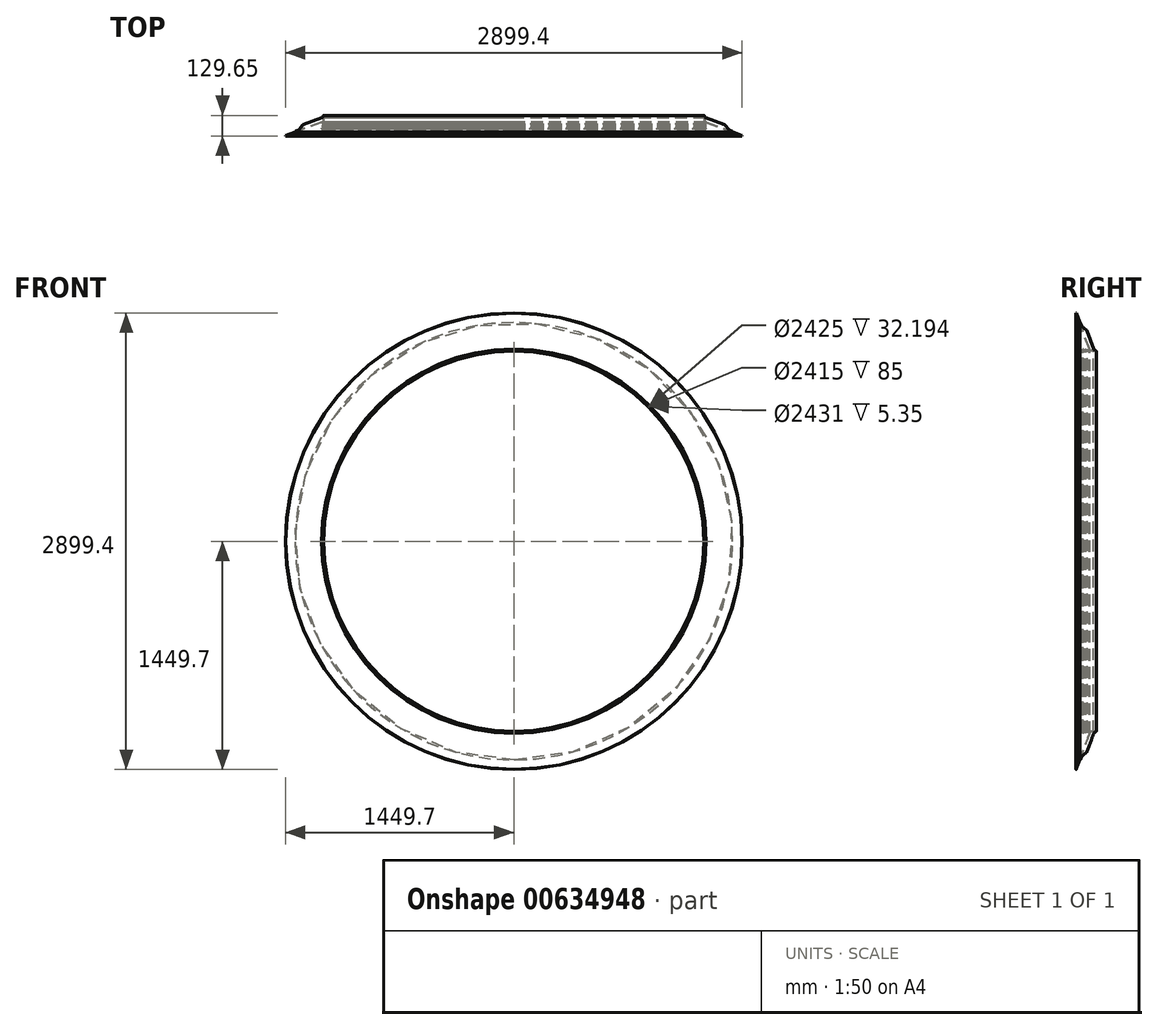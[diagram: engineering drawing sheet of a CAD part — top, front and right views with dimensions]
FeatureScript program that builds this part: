
annotation { "Feature Type Name" : "Feature", "Feature Type Description" : "" }
export const myFeature = defineFeature(function(context is Context, id is Id, definition is map)
    precondition{}
    {
        {
            var Q0;
            Q0=qCreatedBy(makeId("Top.planeOp"),FACE);
            var sketch = newSketch(context, id + "F0", { "sketchPlane" : qUnion([Q0])});
            skLineSegment(sketch, "E0", {"start": v(-64.75, -23.88) * mm, "end": v(-64.75, 61.12) * mm});
            skLineSegment(sketch, "E1", {"start": v(-64.75, -23.88) * mm, "end": v(-52.25, -23.88) * mm});
            skLineSegment(sketch, "E2", {"start": v(-52.25, -23.88) * mm, "end": v(-52.25, -20.88) * mm});
            skLineSegment(sketch, "E3", {"start": v(-54.25, -18.88) * mm, "end": v(-59.75, -18.88) * mm});
            skLineSegment(sketch, "E4", {"start": v(-61.75, -16.88) * mm, "end": v(-61.75, 3.12) * mm});
            skLineSegment(sketch, "E5", {"start": v(-59.75, 5.12) * mm, "end": v(-59.75, 5.12) * mm});
            skLineSegment(sketch, "E6", {"start": v(-59.75, 5.12) * mm, "end": v(-59.75, 42.24) * mm});
            skLineSegment(sketch, "E7", {"start": v(-57.04, 44.1) * mm, "end": v(64.2, -1.46) * mm});
            skLineSegment(sketch, "E8", {"start": v(66.31, -2.99) * mm, "end": v(90, -32.12) * mm});
            skLineSegment(sketch, "E9.0", {"start": v(-54.26, 47.34) * mm, "end": v(66.61, 1.9) * mm});
            skLineSegment(sketch, "E10", {"start": v(-64.75, 61.12) * mm, "end": v(-64.75, 57.12) * mm, "construction": true});
            skArc(sketch, "E11", {"start": v(-64.75, 61.12) * mm, "mid": v(-61.92, 59.95) * mm, "end": v(-60.75, 57.12) * mm});
            skLineSegment(sketch, "E12", {"start": v(-60.75, 57.12) * mm, "end": v(-60.75, 56.7) * mm});
            skArc(sketch, "E13", {"start": v(-60.75, 56.7) * mm, "mid": v(-58.97, 51) * mm, "end": v(-54.26, 47.34) * mm});
            skLineSegment(sketch, "E14.0", {"start": v(68.73, 0.38) * mm, "end": v(92.42, -28.76) * mm});
            skLineSegment(sketch, "E15", {"start": v(94.54, -30.29) * mm, "end": v(114.28, -37.7) * mm});
            skLineSegment(sketch, "E16.0", {"start": v(92.12, -33.65) * mm, "end": v(117.45, -43.17) * mm});
            skArc(sketch, "E17", {"start": v(114.28, -37.7) * mm, "mid": v(116.84, -39.87) * mm, "end": v(117.45, -43.17) * mm});
            skPoint(sketch, "E18.visualSharp", {"position": v(93.27, -29.81) * mm});
            skArc(sketch, "E18.filletArc", {"start": v(92.42, -28.76) * mm, "mid": v(93.37, -29.66) * mm, "end": v(94.54, -30.29) * mm});
            skPoint(sketch, "E19.visualSharp", {"position": v(90.85, -33.17) * mm});
            skArc(sketch, "E19.filletArc", {"start": v(90, -32.12) * mm, "mid": v(90.95, -33.03) * mm, "end": v(92.12, -33.65) * mm});
            skPoint(sketch, "E20.visualSharp", {"position": v(67.88, 1.43) * mm});
            skArc(sketch, "E20.filletArc", {"start": v(68.73, 0.38) * mm, "mid": v(67.78, 1.28) * mm, "end": v(66.61, 1.9) * mm});
            skPoint(sketch, "E21.visualSharp", {"position": v(65.46, -1.93) * mm});
            skArc(sketch, "E21.filletArc", {"start": v(66.31, -2.99) * mm, "mid": v(65.35, -2.08) * mm, "end": v(64.2, -1.46) * mm});
            skPoint(sketch, "E22.visualSharp", {"position": v(-59.75, 45.12) * mm});
            skArc(sketch, "E22.filletArc", {"start": v(-57.04, 44.1) * mm, "mid": v(-58.88, 43.88) * mm, "end": v(-59.75, 42.24) * mm});
            skPoint(sketch, "E23.visualSharp", {"position": v(-61.75, 5.12) * mm});
            skArc(sketch, "E23.filletArc", {"start": v(-59.75, 5.12) * mm, "mid": v(-61.16, 4.54) * mm, "end": v(-61.75, 3.12) * mm});
            skPoint(sketch, "E24.visualSharp", {"position": v(-61.75, -18.88) * mm});
            skArc(sketch, "E24.filletArc", {"start": v(-61.75, -16.88) * mm, "mid": v(-61.16, -18.29) * mm, "end": v(-59.75, -18.88) * mm});
            skPoint(sketch, "E25.visualSharp", {"position": v(-52.25, -18.88) * mm});
            skArc(sketch, "E25.filletArc", {"start": v(-52.25, -20.88) * mm, "mid": v(-52.83, -19.46) * mm, "end": v(-54.25, -18.88) * mm});
            skLineSegment(sketch, "E26", {"start": v(-1272.25, -135.17) * mm, "end": v(-1272.25, 112.51) * mm, "construction": true});
            skSolve(sketch);
        }
        {
            var Q0;
            Q0=qCreatedBy(makeId("Top.planeOp"),FACE);
            var sketch = newSketch(context, id + "F1", { "sketchPlane" : qUnion([Q0])});
            skLineSegment(sketch, "E27", {"start": v(-59.75, -18.88) * mm, "end": v(-59.75, 13.32) * mm});
            skLineSegment(sketch, "E28", {"start": v(-50.28, 19.87) * mm, "end": v(177.45, -65.73) * mm});
            skPoint(sketch, "E29.visualSharp", {"position": v(-59.75, 23.43) * mm});
            skArc(sketch, "E29.filletArc", {"start": v(-50.28, 19.87) * mm, "mid": v(-56.73, 19.07) * mm, "end": v(-59.75, 13.32) * mm});
            skLineSegment(sketch, "E30.0", {"start": v(-51.34, 17.06) * mm, "end": v(176.4, -68.53) * mm});
            skArc(sketch, "E30.1", {"start": v(-51.34, 17.06) * mm, "mid": v(-55.02, 16.6) * mm, "end": v(-56.75, 13.32) * mm});
            skLineSegment(sketch, "E30.2", {"start": v(-56.75, -18.88) * mm, "end": v(-56.75, 13.32) * mm});
            skLineSegment(sketch, "E31", {"start": v(176.4, -68.53) * mm, "end": v(177.45, -65.73) * mm});
            skLineSegment(sketch, "E32", {"start": v(-59.75, -18.88) * mm, "end": v(-56.75, -18.88) * mm});
            skSolve(sketch);
        }
        {
            var Q0;
            Q0=qCreatedBy(makeId("Top.planeOp"),FACE);
            var sketch = newSketch(context, id + "F2", { "sketchPlane" : qUnion([Q0])});
            skLineSegment(sketch, "E33.bottom", {"start": v(-56.75, -8.94) * mm, "end": v(-54.63, -8.94) * mm});
            skLineSegment(sketch, "E33.top", {"start": v(-56.75, -3.59) * mm, "end": v(-54.63, -3.59) * mm});
            skLineSegment(sketch, "E33.left", {"start": v(-56.75, -8.94) * mm, "end": v(-56.75, -3.59) * mm});
            skLineSegment(sketch, "E33.right", {"start": v(-54.63, -8.94) * mm, "end": v(-54.63, -3.59) * mm});
            skSolve(sketch);
        }
        {
            var Q0;
            Q0=makeQuery(id+"F2.imprint","IMPRINT",FACE,{"disambiguationData":[TD([[makeQuery(id+"F2.imprint","IMPRINT",EDGE,{"derivedFrom":sQuery(id+"F2.wireOp",EDGE,"E33.bottom")}),1.0]])]});
            var Q1;
            Q1=sQuery(id+"F0.wireOp",EDGE,"E26");
            revolve(context, id + "F3", {"entities" : qUnion([Q0]), "axis" : qUnion([Q1]), "revolveType" : RevolveType.FULL});
        }
        {
            var Q0;
            Q0=makeQuery(id+"F1.imprint","IMPRINT",FACE,{"disambiguationData":[TD([[makeQuery(id+"F1.imprint","IMPRINT",EDGE,{"derivedFrom":sQuery(id+"F1.wireOp",EDGE,"E27")}),-1.0]])]});
            var Q1;
            Q1=sQuery(id+"F0.wireOp",EDGE,"E26");
            revolve(context, id + "F4", {"entities" : qUnion([Q0]), "axis" : qUnion([Q1]), "revolveType" : RevolveType.FULL});
        }
        {
            var Q0;
            Q0=makeQuery(id+"F0.imprint","IMPRINT",FACE,{"disambiguationData":[TD([[makeQuery(id+"F0.imprint","IMPRINT",EDGE,{"derivedFrom":sQuery(id+"F0.wireOp",EDGE,"E0")}),-1.0]])]});
            var Q1;
            Q1=sQuery(id+"F0.wireOp",EDGE,"E26");
            revolve(context, id + "F5", {"entities" : qUnion([Q0]), "axis" : qUnion([Q1]), "revolveType" : RevolveType.FULL});
        }
    });
